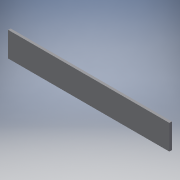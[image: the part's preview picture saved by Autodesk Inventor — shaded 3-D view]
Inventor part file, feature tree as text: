
AUTODESK INVENTOR PART (.ipt)
format: ipt  version: 2019 (Build 230136000, 136)  size: 102,912 bytes
history: native  units: mm
features: extrude x1, sketch x1
ambient origin geometry x8: Origin, YZ Plane, XZ Plane, XY Plane, X Axis, Y Axis, Z Axis, Center Point
bodies: Solid1 (feature_tree)
feature tree (2):
  extrude  "Extrusion1"  Depth=10.0mm
  sketch  "Sketch1"  dims[d0=500.0mm d1=10.0mm d2=500.0mm d3=100.0mm d4=150.0mm d5=100.0mm d6=10.0mm d7=0.0mm]
